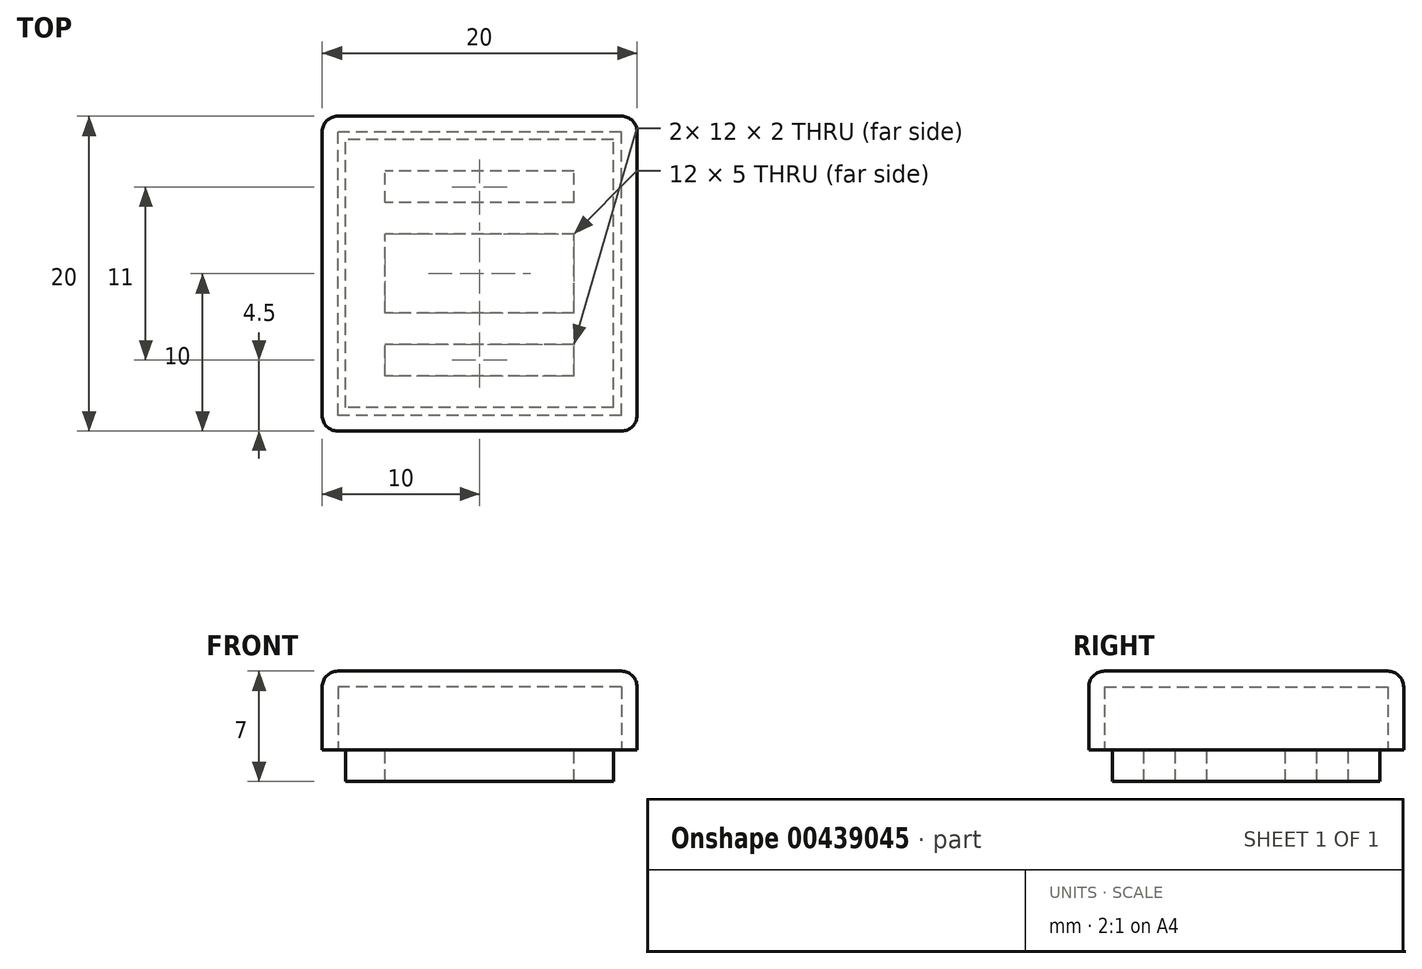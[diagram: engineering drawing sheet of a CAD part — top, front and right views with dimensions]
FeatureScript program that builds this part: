
annotation { "Feature Type Name" : "Feature", "Feature Type Description" : "" }
export const myFeature = defineFeature(function(context is Context, id is Id, definition is map)
    precondition{}
    {
        {
            var Q0;
            Q0=qCreatedBy(makeId("Top.planeOp"),FACE);
            var sketch = newSketch(context, id + "F0", { "sketchPlane" : qUnion([Q0])});
            skLineSegment(sketch, "E0.bottom", {"start": v(10, -10) * mm, "end": v(-10, -10) * mm});
            skLineSegment(sketch, "E0.top", {"start": v(10, 10) * mm, "end": v(-10, 10) * mm});
            skLineSegment(sketch, "E0.left", {"start": v(10, -10) * mm, "end": v(10, 10) * mm});
            skLineSegment(sketch, "E0.right", {"start": v(-10, -10) * mm, "end": v(-10, 10) * mm});
            skPoint(sketch, "E0.middle", {"position": v(0, 0) * mm});
            skSolve(sketch);
        }
        {
            var Q0;
            Q0=qSketchRegion(id+"F0",true);
            extrude(context, id + "F1", {"entities" : qUnion([Q0]), "depth" : 5 * mm});
        }
        {
            var Q0;
            Q0=makeQuery(id+"F1.opExtrude","CAP_FACE",FACE,{"disambiguationData":[OSD([sQuery(id+"F0.wireOp",EDGE,"E0.bottom"),sQuery(id+"F0.wireOp",EDGE,"E0.top"),sQuery(id+"F0.wireOp",EDGE,"E0.left"),sQuery(id+"F0.wireOp",EDGE,"E0.right")])],"isStart":true});
            shell(context, id + "F2", {"entities" : qUnion([Q0]), "thickness" : 1 * mm});
        }
        {
            var Q0;
            Q0=makeQuery(id+"F1.opExtrude","CAP_FACE",FACE,{"disambiguationData":[OSD([sQuery(id+"F0.wireOp",EDGE,"E0.bottom"),sQuery(id+"F0.wireOp",EDGE,"E0.top"),sQuery(id+"F0.wireOp",EDGE,"E0.left"),sQuery(id+"F0.wireOp",EDGE,"E0.right")])],"isStart":false});
            var Q1;
            Q1=makeQuery(id+"F1.opExtrude","SWEPT_EDGE",EDGE,{"disambiguationData":[OSD([sQuery(id+"F0.wireOp",EDGE,"E0.bottom"),sQuery(id+"F0.wireOp",EDGE,"E0.right")])]});
            var Q2;
            Q2=makeQuery(id+"F1.opExtrude","SWEPT_EDGE",EDGE,{"disambiguationData":[OSD([sQuery(id+"F0.wireOp",EDGE,"E0.bottom"),sQuery(id+"F0.wireOp",EDGE,"E0.left")])]});
            var Q3;
            Q3=makeQuery(id+"F1.opExtrude","SWEPT_EDGE",EDGE,{"disambiguationData":[OSD([sQuery(id+"F0.wireOp",EDGE,"E0.top"),sQuery(id+"F0.wireOp",EDGE,"E0.left")])]});
            var Q4;
            Q4=makeQuery(id+"F1.opExtrude","SWEPT_EDGE",EDGE,{"disambiguationData":[OSD([sQuery(id+"F0.wireOp",EDGE,"E0.top"),sQuery(id+"F0.wireOp",EDGE,"E0.right")])]});
            fillet(context, id + "F3", {"entities" : qUnion([Q0, Q1, Q2, Q3, Q4]), "radius" : 1 * mm, "tangentPropagation" : true, "allowEdgeOverflow" : false});
        }
        {
            var Q0;
            Q0=qCreatedBy(makeId("Top.planeOp"),FACE);
            var sketch = newSketch(context, id + "F4", { "sketchPlane" : qUnion([Q0])});
            skLineSegment(sketch, "E1.bottom", {"start": v(8.5, -8.5) * mm, "end": v(-8.5, -8.5) * mm});
            skLineSegment(sketch, "E1.top", {"start": v(8.5, 8.5) * mm, "end": v(-8.5, 8.5) * mm});
            skLineSegment(sketch, "E1.left", {"start": v(8.5, -8.5) * mm, "end": v(8.5, 8.5) * mm});
            skLineSegment(sketch, "E1.right", {"start": v(-8.5, -8.5) * mm, "end": v(-8.5, 8.5) * mm});
            skPoint(sketch, "E1.middle", {"position": v(0, 0) * mm});
            skLineSegment(sketch, "E2.bottom", {"start": v(6, -2.5) * mm, "end": v(-6, -2.5) * mm});
            skLineSegment(sketch, "E2.top", {"start": v(6, 2.5) * mm, "end": v(-6, 2.5) * mm});
            skLineSegment(sketch, "E2.left", {"start": v(6, -2.5) * mm, "end": v(6, 2.5) * mm});
            skLineSegment(sketch, "E2.right", {"start": v(-6, -2.5) * mm, "end": v(-6, 2.5) * mm});
            skLineSegment(sketch, "E3.bottom", {"start": v(6, 4.5) * mm, "end": v(-6, 4.5) * mm});
            skLineSegment(sketch, "E3.top", {"start": v(6, 6.5) * mm, "end": v(-6, 6.5) * mm});
            skLineSegment(sketch, "E3.left", {"start": v(6, 4.5) * mm, "end": v(6, 6.5) * mm});
            skLineSegment(sketch, "E3.right", {"start": v(-6, 4.5) * mm, "end": v(-6, 6.5) * mm});
            skPoint(sketch, "E3.middle", {"position": v(0, 5.5) * mm});
            skLineSegment(sketch, "E4.bottom", {"start": v(6, -6.5) * mm, "end": v(-6, -6.5) * mm});
            skLineSegment(sketch, "E4.top", {"start": v(6, -4.5) * mm, "end": v(-6, -4.5) * mm});
            skLineSegment(sketch, "E4.left", {"start": v(6, -6.5) * mm, "end": v(6, -4.5) * mm});
            skLineSegment(sketch, "E4.right", {"start": v(-6, -6.5) * mm, "end": v(-6, -4.5) * mm});
            skPoint(sketch, "E4.middle", {"position": v(0, -5.5) * mm});
            skLineSegment(sketch, "E5", {"start": v(-6.23, 3.5) * mm, "end": v(6.3, 3.5) * mm, "construction": true});
            skLineSegment(sketch, "E6", {"start": v(-6.74, -3.5) * mm, "end": v(5.67, -3.5) * mm, "construction": true});
            skSolve(sketch);
        }
        {
            var Q0;
            Q0=qSketchRegion(id+"F4",true);
            extrude(context, id + "F5", {"entities" : qUnion([Q0]), "oppositeDirection" : true, "depth" : 2 * mm});
        }
    });
